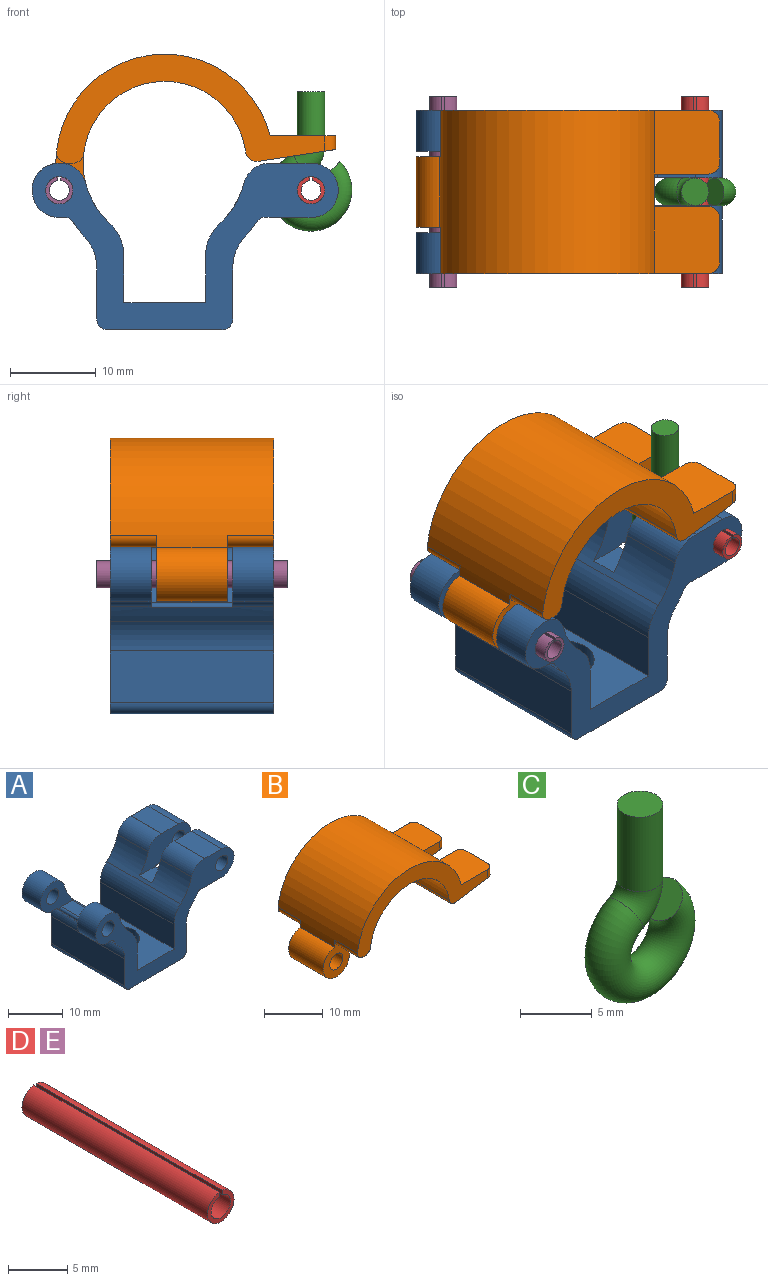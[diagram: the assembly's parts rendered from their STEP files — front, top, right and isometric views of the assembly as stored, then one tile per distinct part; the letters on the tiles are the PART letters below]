
ASSEMBLY  parts=5 mates=4
PART A: 48 faces, bbox 35.7x19.1x19.4 mm
  f0: plane 7.91x4.36mm, normal (0,0,1), area 34.5mm2, adj f22,f24,f31,f45
  f1: cylinder r=3.17mm len=7.89mm, axis (0,1,0), area 3.2mm2, adj f2,f8,f32,f44
  f2: plane 7.89x4.76mm, normal (0,0,-1), area 37.6mm2, adj f1,f3,f32,f44
  f3: cylinder r=3.17mm len=7.89mm, axis (0,1,0), area 78.7mm2, adj f2,f23,f32,f44
  f4: cylinder r=12.7mm len=7.89mm, axis (0,1,0), area 0.2mm2, adj f5,f23,f32,f44
  f5: cylinder r=3.17mm len=7.89mm, axis (0,1,0), area 36.2mm2, adj f4,f6,f32,f44
  f6: cylinder r=9.53mm len=19.05mm, axis (0,1,0), area 89.5mm2, adj f5,f25,f31,f32,f36,f43,f44,f45
  f7: cylinder r=1.59mm len=7.89mm, axis (0,1,0), area 78.7mm2, adj f32,f44
  f8: cylinder r=1.27mm len=19.05mm, axis (0,-1,0), area 24.3mm2, adj f1,f19,f20,f31,f32,f43,f44,f45
  f9: cylinder r=1.27mm len=4.78mm, axis (0,-1,0), area 6.8mm2, adj f14,f15,f31,f40
  f10: cylinder r=3.17mm len=6.35mm, axis (0,1,0), area 69.2mm2, adj f12,f13,f32,f39
  f11: cylinder r=1.59mm len=4.75mm, axis (0,1,0), area 47.4mm2, adj f32,f39
  f12: cylinder r=9.53mm len=19.05mm, axis (0,1,0), area 57.6mm2, adj f10,f14,f31,f32,f37,f39,f40,f41
  f13: cylinder r=1.27mm len=4.75mm, axis (0,-1,0), area 6.8mm2, adj f10,f15,f32,f39
  f14: cylinder r=3.17mm len=6.35mm, axis (0,1,0), area 69.5mm2, adj f9,f12,f31,f40
  f15: cylinder r=12.7mm len=19.05mm, axis (0,1,0), area 40.5mm2, adj f9,f13,f31,f32,f34,f39,f40,f42
  f16: plane 19.05x6.06mm, normal (-1,0,0), area 115.4mm2, adj f31,f32,f34,f46
  f17: plane 19.05x13.34mm, normal (0,0,-1), area 208.4mm2, adj f31,f32,f33,f46,f47
  f18: plane 19.05x6.06mm, normal (1,0,0), area 115.4mm2, adj f31,f32,f35,f47
  f19: cylinder r=12.7mm len=19.05mm, axis (0,1,0), area 42.5mm2, adj f8,f31,f32,f35
  f20: cylinder r=3.17mm len=7.91mm, axis (0,1,0), area 3.2mm2, adj f8,f21,f31,f45
  f21: plane 7.91x4.76mm, normal (0,0,-1), area 37.7mm2, adj f20,f22,f31,f45
  f22: cylinder r=3.17mm len=7.91mm, axis (0,1,0), area 78.9mm2, adj f0,f21,f31,f45
  f23: plane 7.89x4.36mm, normal (0,0,1), area 34.4mm2, adj f3,f4,f32,f44
  f24: cylinder r=12.7mm len=7.91mm, axis (0,1,0), area 0.2mm2, adj f0,f25,f31,f45
  f25: cylinder r=3.17mm len=7.91mm, axis (0,1,0), area 36.3mm2, adj f6,f24,f31,f45
  f26: plane 19.05x5.47mm, normal (-1,0,0), area 104.3mm2, adj f27,f31,f32,f36
  f27: plane 19.05x9.53mm, normal (0,0,1), area 135.8mm2, adj f26,f28,f31,f32,f33
  f28: plane 19.05x5.47mm, normal (1,0,0), area 104.3mm2, adj f27,f31,f32,f37
  f29: cylinder r=1.59mm len=4.78mm, axis (0,1,0), area 47.6mm2, adj f31,f40
  f30: cylinder r=1.59mm len=7.91mm, axis (0,1,0), area 78.9mm2, adj f31,f45
  f31: plane 35.71x19.44mm, normal (0,-1,0), area 207.7mm2, adj f0,f6,f8,f9,f12,f14,f15,f16
  f32: plane 35.71x19.44mm, normal (0,1,0), area 207.7mm2, adj f1,f2,f3,f4,f5,f6,f7,f8
  f33: cylinder r=3.81mm len=7.62mm, axis (0,0,1), area 76mm2, adj f17,f27
  f34: cylinder r=5.08mm len=19.05mm, axis (0,1,0), area 72.5mm2, adj f15,f16,f31,f32
  f35: cylinder r=5.08mm len=19.05mm, axis (0,1,0), area 72.5mm2, adj f18,f19,f31,f32
  f36: cylinder r=5.08mm len=19.05mm, axis (0,1,0), area 80.4mm2, adj f6,f26,f31,f32
  f37: cylinder r=5.08mm len=19.05mm, axis (0,1,0), area 80.4mm2, adj f12,f28,f31,f32
  f38: plane 9.53x2.88mm, normal (0,0,1), area 27.4mm2, adj f39,f40,f41,f42
  f39: plane 8.67x7.07mm, normal (0,-1,0), area 29.8mm2, adj f10,f11,f12,f13,f15,f38,f41,f42
  f40: plane 8.67x7.07mm, normal (0,1,0), area 29.8mm2, adj f9,f12,f14,f15,f29,f38,f41,f42
  f41: cylinder r=0.51mm len=9.53mm, axis (0,1,0), area 3.8mm2, adj f12,f38,f39,f40
  f42: cylinder r=0.51mm len=9.53mm, axis (0,-1,0), area 8mm2, adj f15,f38,f39,f40
  f43: plane 4.1x3.25mm, normal (0,0,1), area 13.3mm2, adj f6,f8,f44,f45
  f44: plane 13.28x6.51mm, normal (0,-1,0), area 59.9mm2, adj f1,f2,f3,f4,f5,f6,f7,f8
  f45: plane 13.28x6.51mm, normal (0,1,0), area 59.9mm2, adj f0,f6,f8,f20,f21,f22,f24,f25
  f46: cylinder r=1.27mm len=19.05mm, axis (0,1,0), area 38mm2, adj f16,f17,f31,f32
  f47: cylinder r=1.27mm len=19.05mm, axis (0,-1,0), area 38mm2, adj f17,f18,f31,f32
PART B: 27 faces, bbox 35.4x19.1x19.1 mm
  f0: cylinder r=12.7mm len=25mm, axis (0,1,0), area 683.9mm2, adj f1,f3,f4,f6,f9,f11,f14,f16
  f1: cylinder r=3.17mm len=8.26mm, axis (0,1,0), area 126.8mm2, adj f0,f2,f14,f16
  f2: cylinder r=9.53mm len=19.05mm, axis (0,1,0), area 553.1mm2, adj f1,f3,f4,f14,f16,f19,f21,f24
  f3: plane 31.28x12.7mm, normal (0,-1,0), area 122.7mm2, adj f0,f2,f6,f7,f13,f18,f19,f24
  f4: plane 31.28x12.7mm, normal (0,1,0), area 122.7mm2, adj f0,f2,f7,f9,f15,f20,f21,f24
  f5: plane 5.26x1.59mm, normal (1,0,0), area 8.4mm2, adj f6,f7,f23,f26
  f6: plane 7.8x7.62mm, normal (0,0,1), area 58.8mm2, adj f0,f3,f5,f12,f23,f26
  f7: plane 19.05x9.03mm, normal (0.15,0,-0.99), area 143.2mm2, adj f3,f4,f5,f8,f10,f11,f12,f22
  f8: plane 4.9x1.59mm, normal (1,0,0), area 7.8mm2, adj f7,f9,f22,f25
  f9: plane 7.62x7.44mm, normal (0,0,1), area 56mm2, adj f0,f4,f8,f10,f22,f25
  f10: plane 6.35x2.75mm, normal (0,-1,0), area 14.4mm2, adj f7,f9,f11,f22
  f11: plane 3.81x2.75mm, normal (1,0,0), area 10.5mm2, adj f0,f7,f10,f12
  f12: plane 6.35x2.75mm, normal (0,1,0), area 14.4mm2, adj f6,f7,f11,f23
  f13: plane 5.4x0.64mm, normal (0,0,-1), area 3.5mm2, adj f3,f14,f18,f19
  f14: plane 7.76x6.35mm, normal (0,-1,0), area 25.9mm2, adj f0,f1,f2,f13,f17,f18,f19
  f15: plane 5.4x0.64mm, normal (0,0,-1), area 3.5mm2, adj f4,f16,f20,f21
  f16: plane 7.76x6.35mm, normal (0,1,0), area 25.9mm2, adj f0,f1,f2,f15,f17,f20,f21
  f17: cylinder r=1.59mm len=8.26mm, axis (0,1,0), area 82.3mm2, adj f14,f16
  f18: cylinder r=1.27mm len=5.4mm, axis (0,1,0), area 11.5mm2, adj f0,f3,f13,f14
  f19: cylinder r=1.27mm len=5.4mm, axis (0,1,0), area 10mm2, adj f2,f3,f13,f14
  f20: cylinder r=1.27mm len=5.4mm, axis (0,1,0), area 11.5mm2, adj f0,f4,f15,f16
  f21: cylinder r=1.27mm len=5.4mm, axis (0,1,0), area 10mm2, adj f2,f4,f15,f16
  f22: cylinder r=1.27mm len=1.78mm, axis (0,0,-1), area 3.3mm2, adj f7,f8,f9,f10
  f23: cylinder r=1.27mm len=1.78mm, axis (0,0,1), area 3.3mm2, adj f5,f6,f7,f12
  f24: cylinder r=1.27mm len=19.05mm, axis (0,1,0), area 38.4mm2, adj f2,f3,f4,f7
  f25: cylinder r=1.27mm len=1.78mm, axis (0,0,1), area 3.3mm2, adj f4,f7,f8,f9
  f26: cylinder r=1.27mm len=1.78mm, axis (0,0,-1), area 3.3mm2, adj f3,f5,f6,f7
PART C: 5 faces, bbox 10.3x3.2x16.6 mm
  f0: plane 3.18x3.18mm, normal (0,0,1), area 7.9mm2, adj f2
  f1: plane 3.18x2.25mm, normal (-0.71,0,0.71), area 7.9mm2, adj f4
  f2: cylinder r=1.59mm len=6.35mm, axis (0,0,-1), area 63.3mm2, adj f0,f3
  f3: torus R=2.54mm, axis (0,1,0), area 28.1mm2, adj f2,f4
  f4: torus R=3.17mm, axis (0,-1,0), area 159.5mm2, adj f1,f3
PART D: 6 faces, bbox 3.2x22.2x3.2 mm
  f0: plane 22.23x0.44mm, normal (1,0,0), area 9.7mm2, adj f1,f3,f4,f5
  f1: cylinder r=1.59mm len=22.23mm, axis (0,1,0), area 214.6mm2, adj f0,f2,f4,f5
  f2: plane 22.23x0.44mm, normal (-1,0,0), area 9.7mm2, adj f1,f3,f4,f5
  f3: cylinder r=1.16mm len=22.23mm, axis (0,1,0), area 154.2mm2, adj f0,f2,f4,f5
  f4: plane 3.18x3.17mm, normal (0,-1,0), area 3.6mm2, adj f0,f1,f2,f3
  f5: plane 3.18x3.17mm, normal (0,1,0), area 3.6mm2, adj f0,f1,f2,f3
PART E: same geometry as D
PLACE A rot(axis=(0.05,0.06,1),0deg) t=(-43.63,21.37,-6.63)mm fixed
PLACE B t=(-43.63,21.37,-6.63)mm
PLACE C rot(axis=(0.05,0.06,1),0deg) t=(-73.34,11.85,-51.36)mm
PLACE D rot(axis=(0.05,0.06,1),0deg) t=(-14.27,42.01,-6.63)mm
PLACE E rot(axis=(0.05,0.06,1),0deg) t=(-43.63,42.01,-6.63)mm
MATE fastened D.f1 <-> A.f3  axis (0,-1,0) through (-26.57,0.73,-9.81)mm
MATE fastened E.f1 <-> A.f10  axis (0,-1,0) through (-55.92,0.73,-9.81)mm
MATE revolute B.f1 <-> E.f1  axis (0,1,0) through (-55.92,11.85,-9.81)mm
MATE revolute C.f4 <-> D.f1  axis (0,-1,0) through (-26.57,11.85,-9.81)mm
